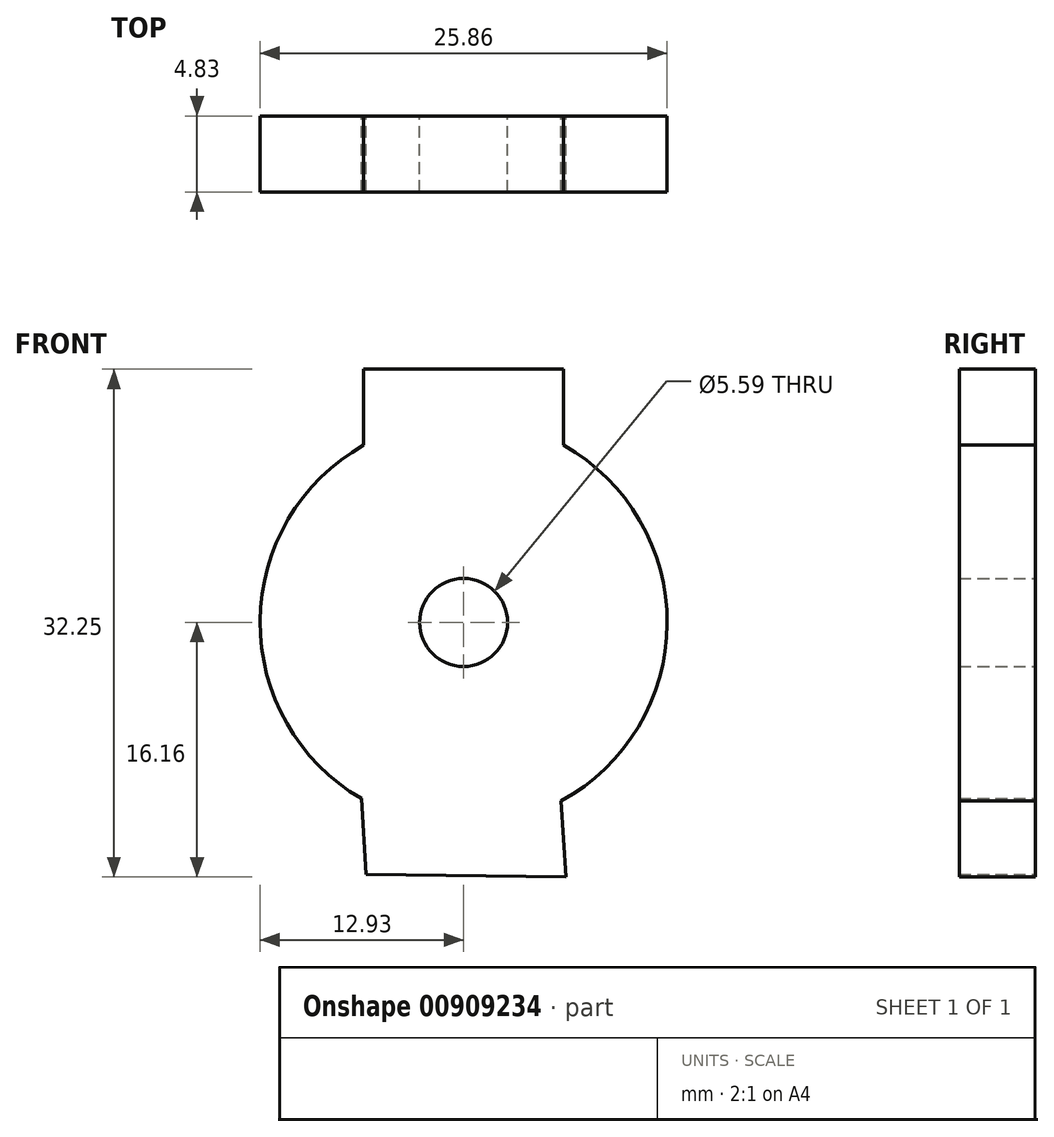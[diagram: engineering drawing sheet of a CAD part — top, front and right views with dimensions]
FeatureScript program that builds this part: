
annotation { "Feature Type Name" : "Feature", "Feature Type Description" : "" }
export const myFeature = defineFeature(function(context is Context, id is Id, definition is map)
    precondition{}
    {
        {
            var Q0;
            Q0=qCreatedBy(makeId("Front.planeOp"),FACE);
            var sketch = newSketch(context, id + "F0", { "sketchPlane" : qUnion([Q0])});
            skLineSegment(sketch, "E0.bottom", {"start": v(6.5, -16.16) * mm, "end": v(-6.2, -16) * mm});
            skLineSegment(sketch, "E0.left", {"start": v(6.5, -16.16) * mm, "end": v(6.2, -11.34) * mm});
            skLineSegment(sketch, "E0.right", {"start": v(-6.2, -16) * mm, "end": v(-6.5, -11.18) * mm});
            skPoint(sketch, "E0.middle", {"position": v(0, -13.67) * mm});
            skArc(sketch, "E1", {"start": v(6.2, -11.34) * mm, "mid": v(12.93, -0.09) * mm, "end": v(6.35, 11.26) * mm});
            skPoint(sketch, "E2.center", {"position": v(0, -0.04) * mm});
            skLineSegment(sketch, "E3.top", {"start": v(6.35, 16.09) * mm, "end": v(-6.35, 16.09) * mm});
            skLineSegment(sketch, "E3.left", {"start": v(6.35, 11.26) * mm, "end": v(6.35, 16.09) * mm});
            skLineSegment(sketch, "E3.right", {"start": v(-6.35, 11.26) * mm, "end": v(-6.35, 16.09) * mm});
            skPoint(sketch, "E3.middle", {"position": v(0, 13.67) * mm});
            skCircle(sketch, "E4", {"center": v(0, 0) * mm, "radius": 2.8 * mm});
            skArc(sketch, "E5.trimOffspring", {"start": v(-6.35, 11.26) * mm, "mid": v(-12.93, 0.09) * mm, "end": v(-6.5, -11.18) * mm});
            skSolve(sketch);
        }
        {
            var Q0;
            Q0=makeQuery(id+"F0.imprint","IMPRINT",FACE,{"disambiguationData":[TD([[makeQuery(id+"F0.imprint","IMPRINT",EDGE,{"derivedFrom":sQuery(id+"F0.wireOp",EDGE,"E0.bottom")}),-1.0]])]});
            extrude(context, id + "F1", {"entities" : qUnion([Q0]), "depth" : 4.83 * mm, "offsetDistance" : 25.4 * mm});
        }
    });
